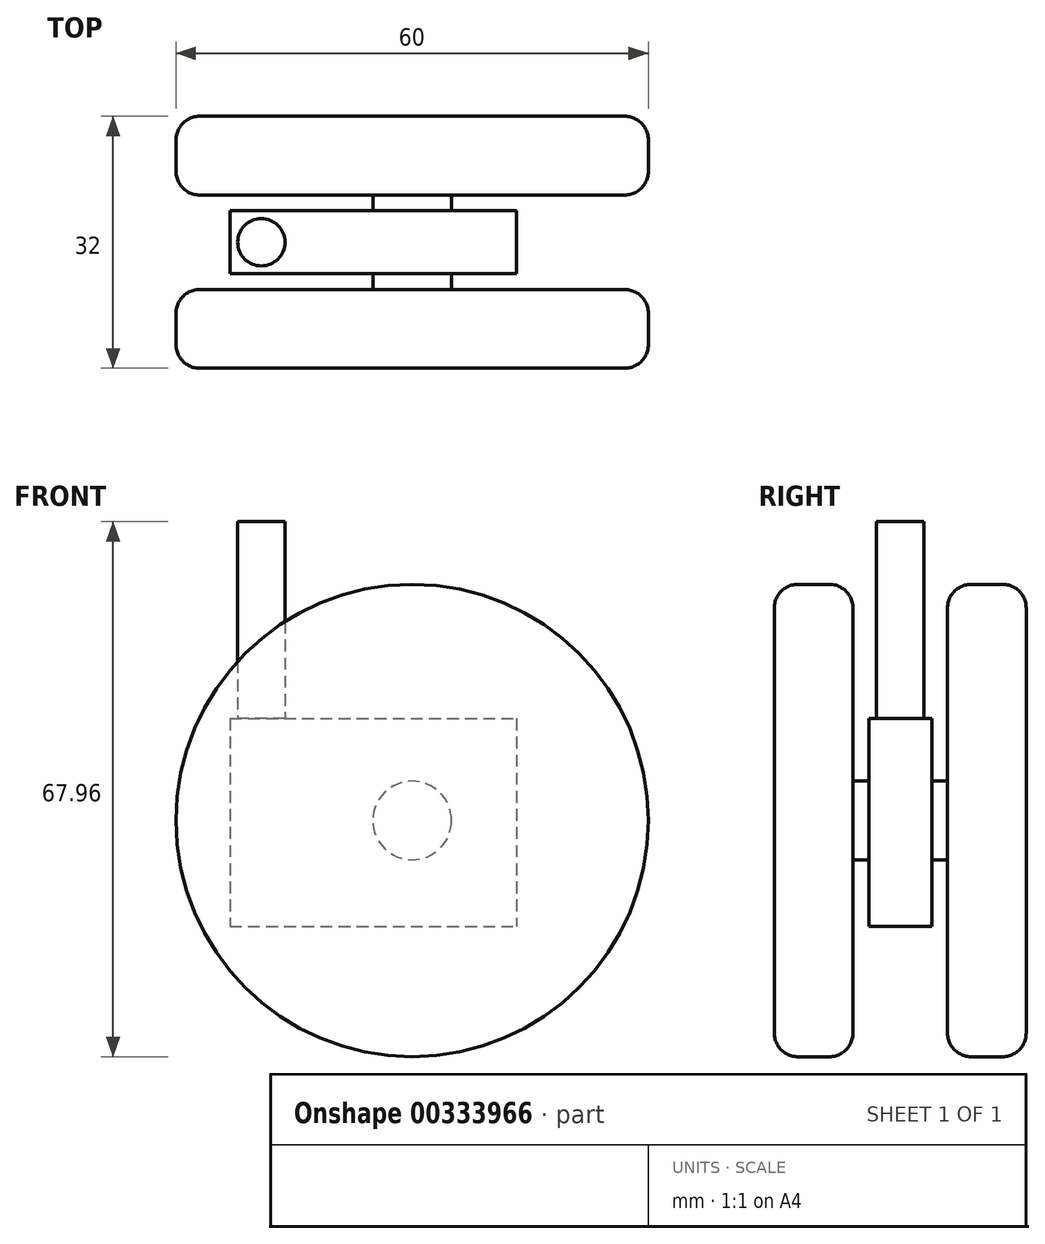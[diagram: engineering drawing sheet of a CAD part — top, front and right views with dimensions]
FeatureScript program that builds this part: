
annotation { "Feature Type Name" : "Feature", "Feature Type Description" : "" }
export const myFeature = defineFeature(function(context is Context, id is Id, definition is map)
    precondition{}
    {
        {
            var Q0;
            Q0=qCreatedBy(makeId("Front.planeOp"),FACE);
            var sketch = newSketch(context, id + "F0", { "sketchPlane" : qUnion([Q0])});
            skCircle(sketch, "E0", {"center": v(0, 0) * mm, "radius": 30 * mm});
            skSolve(sketch);
        }
        {
            var Q0;
            Q0=makeQuery(id+"F0.imprint","IMPRINT",FACE,{"disambiguationData":[TD([[makeQuery(id+"F0.imprint","IMPRINT",EDGE,{"derivedFrom":sQuery(id+"F0.wireOp",EDGE,"E0")}),1.0]])]});
            extrude(context, id + "F1", {"entities" : qUnion([Q0]), "depth" : 10 * mm});
        }
        {
            var Q0;
            Q0=makeQuery(id+"F1.opExtrude","SWEPT_FACE",FACE,{"disambiguationData":[OSD([sQuery(id+"F0.wireOp",EDGE,"E0")])]});
            fillet(context, id + "F2", {"entities" : qUnion([Q0]), "radius" : 3 * mm, "tangentPropagation" : true, "allowEdgeOverflow" : false});
        }
        {
            var Q0;
            Q0=makeQuery(id+"F1.opExtrude","CAP_FACE",FACE,{"disambiguationData":[OSD([sQuery(id+"F0.wireOp",EDGE,"E0")])],"isStart":false});
            var sketch = newSketch(context, id + "F3", { "sketchPlane" : qUnion([Q0])});
            skCircle(sketch, "E1", {"center": v(0, 0) * mm, "radius": 5 * mm});
            skSolve(sketch);
        }
        {
            var Q0;
            Q0 = qSketchRegion(id + "F3", true);
            extrude(context, id + "F4", {"entities" : qUnion([Q0]), "operationType" : NewBodyOperationType.ADD, "depth" : 6 * mm});
        }
        {
            var Q0;
            Q0=makeQuery(id+"F1.opExtrude","SWEPT_BODY",BODY,{"disambiguationData":[OSD([sQuery(id+"F0.wireOp",EDGE,"E0")])]});
            var Q1;
            Q1=makeQuery(id+"F4.opExtrude","CAP_FACE",FACE,{"disambiguationData":[OSD([sQuery(id+"F3.wireOp",EDGE,"E1")])],"isStart":false});
            mirror(context, id + "F5", {"entities" : qUnion([Q0]), "mirrorPlane" : qUnion([Q1])});
        }
        {
            var Q0;
            Q0=makeQuery(id+"F4.opExtrude","CAP_FACE",FACE,{"disambiguationData":[OSD([sQuery(id+"F3.wireOp",EDGE,"E1")])],"isStart":false});
            var sketch = newSketch(context, id + "F6", { "sketchPlane" : qUnion([Q0])});
            skLineSegment(sketch, "E2.bottom", {"start": v(-23.16, 12.96) * mm, "end": v(13.28, 12.96) * mm});
            skLineSegment(sketch, "E2.top", {"start": v(-23.16, -13.44) * mm, "end": v(13.28, -13.44) * mm});
            skLineSegment(sketch, "E2.left", {"start": v(-23.16, 12.96) * mm, "end": v(-23.16, -13.44) * mm});
            skLineSegment(sketch, "E2.right", {"start": v(13.28, 12.96) * mm, "end": v(13.28, -13.44) * mm});
            skSolve(sketch);
        }
        {
            var Q0;
            Q0=makeQuery(id+"F6.imprint","IMPRINT",FACE,{"disambiguationData":[TD([[makeQuery(id+"F6.imprint","IMPRINT",EDGE,{"derivedFrom":sQuery(id+"F6.wireOp",EDGE,"E2.bottom")}),-1.0]])]});
            extrude(context, id + "F7", {"entities" : qUnion([Q0]), "operationType" : NewBodyOperationType.ADD, "endBound" : BoundingType.SYMMETRIC, "depth" : 8 * mm});
        }
        {
            var Q0;
            Q0=makeQuery(id+"F7.opExtrude","SWEPT_FACE",FACE,{"disambiguationData":[OSD([sQuery(id+"F6.wireOp",EDGE,"E2.bottom")])]});
            var sketch = newSketch(context, id + "F8", { "sketchPlane" : qUnion([Q0])});
            skLineSegment(sketch, "E3", {"start": v(-19.16, -20) * mm, "end": v(-19.16, -12) * mm, "construction": true});
            skCircle(sketch, "E4", {"center": v(-19.16, -16) * mm, "radius": 3 * mm});
            skSolve(sketch);
        }
        {
            var Q0;
            Q0 = qSketchRegion(id + "F8", true);
            extrude(context, id + "F9", {"entities" : qUnion([Q0]), "operationType" : NewBodyOperationType.ADD, "depth" : 25 * mm});
        }
    });
